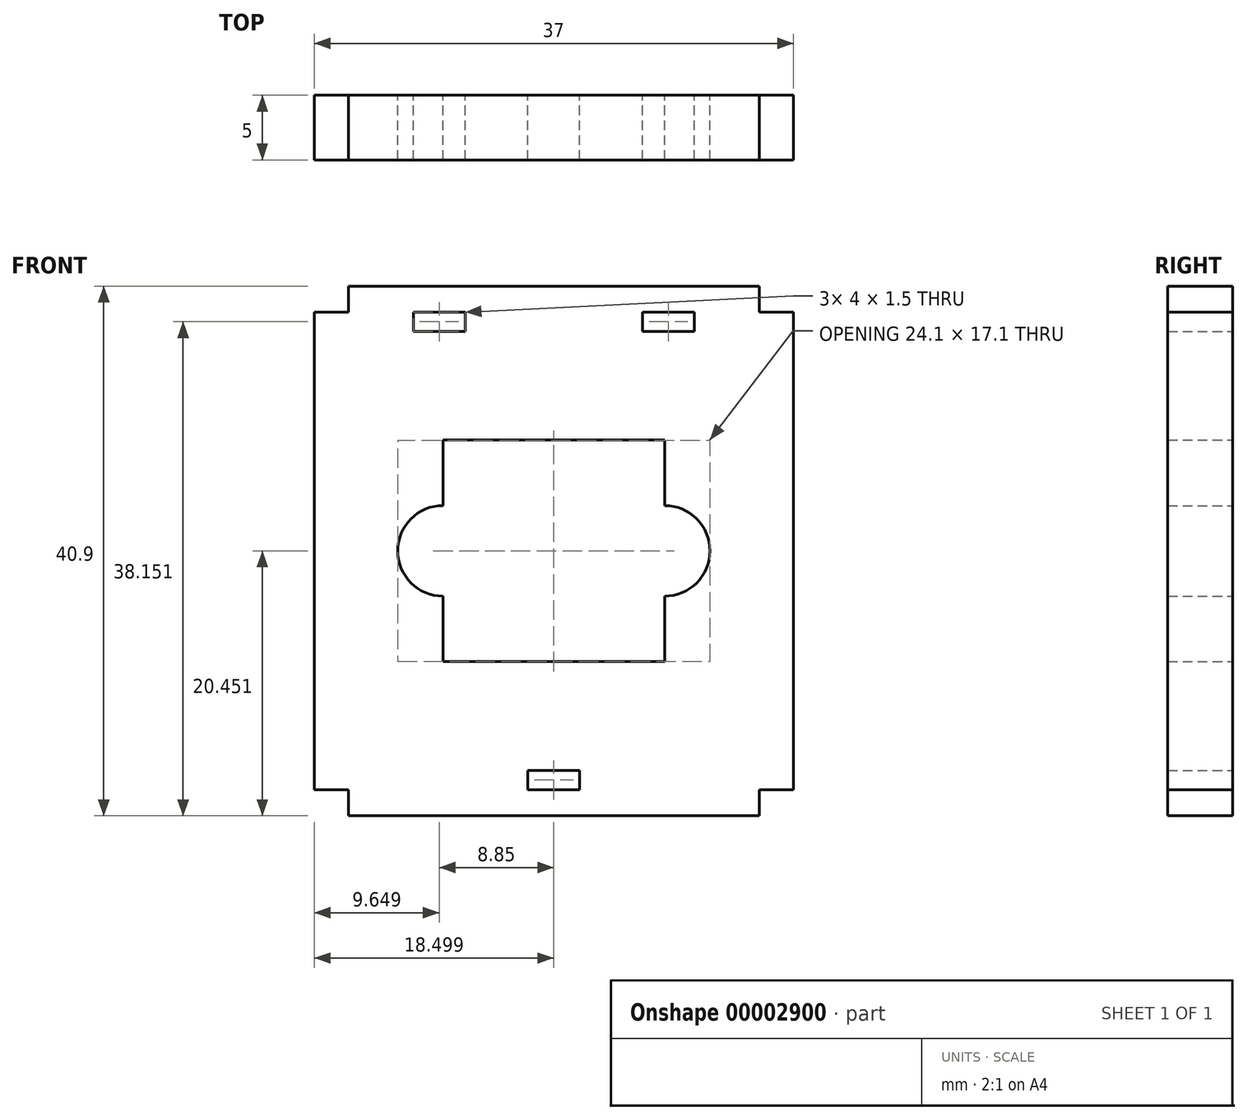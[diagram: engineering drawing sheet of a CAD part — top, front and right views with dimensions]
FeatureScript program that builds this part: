
annotation { "Feature Type Name" : "Feature", "Feature Type Description" : "" }
export const myFeature = defineFeature(function(context is Context, id is Id, definition is map)
    precondition{}
    {
        {
            var Q0;
            Q0=qCreatedBy(makeId("Front.planeOp"),FACE);
            var sketch = newSketch(context, id + "F0", { "sketchPlane" : qUnion([Q0])});
            skLineSegment(sketch, "E0.bottom", {"start": v(-37.5, 13.27) * mm, "end": v(-20.4, 13.27) * mm});
            skLineSegment(sketch, "E0.top", {"start": v(-37.5, -3.83) * mm, "end": v(-20.4, -3.83) * mm});
            skLineSegment(sketch, "E0.left", {"start": v(-37.5, 13.27) * mm, "end": v(-37.5, 8.22) * mm});
            skLineSegment(sketch, "E0.right", {"start": v(-20.4, 13.27) * mm, "end": v(-20.4, 8.22) * mm});
            skArc(sketch, "E1", {"start": v(-37.5, 8.22) * mm, "mid": v(-41, 4.72) * mm, "end": v(-37.5, 1.22) * mm});
            skArc(sketch, "E2", {"start": v(-20.4, 1.22) * mm, "mid": v(-16.9, 4.72) * mm, "end": v(-20.4, 8.22) * mm});
            skLineSegment(sketch, "E3.trimOffspring", {"start": v(-37.5, 1.22) * mm, "end": v(-37.5, -3.83) * mm});
            skLineSegment(sketch, "E4.trimOffspring", {"start": v(-20.4, 1.22) * mm, "end": v(-20.4, -3.83) * mm});
            skLineSegment(sketch, "E5.bottom", {"start": v(-47.45, 23.17) * mm, "end": v(-44.8, 23.17) * mm});
            skLineSegment(sketch, "E5.top", {"start": v(-47.45, -13.73) * mm, "end": v(-44.8, -13.73) * mm});
            skLineSegment(sketch, "E5.left", {"start": v(-47.45, 23.17) * mm, "end": v(-47.45, -13.73) * mm});
            skLineSegment(sketch, "E5.right", {"start": v(-10.45, 23.17) * mm, "end": v(-10.45, -13.73) * mm});
            skLineSegment(sketch, "E6.top", {"start": v(-44.8, 25.17) * mm, "end": v(-13.1, 25.17) * mm});
            skLineSegment(sketch, "E6.left", {"start": v(-44.8, 23.17) * mm, "end": v(-44.8, 25.17) * mm});
            skLineSegment(sketch, "E6.right", {"start": v(-13.1, 23.17) * mm, "end": v(-13.1, 25.17) * mm});
            skLineSegment(sketch, "E7.top", {"start": v(-44.8, -15.73) * mm, "end": v(-13.1, -15.73) * mm});
            skLineSegment(sketch, "E7.left", {"start": v(-44.8, -13.73) * mm, "end": v(-44.8, -15.73) * mm});
            skLineSegment(sketch, "E7.right", {"start": v(-13.1, -13.73) * mm, "end": v(-13.1, -15.73) * mm});
            skLineSegment(sketch, "E8.trimOffspring", {"start": v(-13.1, 23.17) * mm, "end": v(-10.45, 23.17) * mm});
            skLineSegment(sketch, "E9.trimOffspring", {"start": v(-13.1, -13.73) * mm, "end": v(-10.45, -13.73) * mm});
            skLineSegment(sketch, "E10", {"start": v(-28.95, 13.27) * mm, "end": v(-28.95, -3.83) * mm, "construction": true});
            skLineSegment(sketch, "E11.bottom", {"start": v(-39.8, 23.17) * mm, "end": v(-35.8, 23.17) * mm});
            skLineSegment(sketch, "E11.top", {"start": v(-39.8, 21.67) * mm, "end": v(-35.8, 21.67) * mm});
            skLineSegment(sketch, "E11.left", {"start": v(-39.8, 23.17) * mm, "end": v(-39.8, 21.67) * mm});
            skLineSegment(sketch, "E11.right", {"start": v(-35.8, 23.17) * mm, "end": v(-35.8, 21.67) * mm});
            skLineSegment(sketch, "E12.0.MirrorCS", {"start": v(-18.1, 23.17) * mm, "end": v(-22.1, 23.17) * mm});
            skLineSegment(sketch, "E12.1.MirrorCS", {"start": v(-22.1, 23.17) * mm, "end": v(-22.1, 21.67) * mm});
            skLineSegment(sketch, "E12.2.MirrorCS", {"start": v(-18.1, 23.17) * mm, "end": v(-18.1, 21.67) * mm});
            skLineSegment(sketch, "E12.3.MirrorCS", {"start": v(-18.1, 21.67) * mm, "end": v(-22.1, 21.67) * mm});
            skLineSegment(sketch, "E13.bottom", {"start": v(-30.95, -13.73) * mm, "end": v(-26.95, -13.73) * mm});
            skLineSegment(sketch, "E13.top", {"start": v(-30.95, -12.23) * mm, "end": v(-26.95, -12.23) * mm});
            skLineSegment(sketch, "E13.left", {"start": v(-30.95, -13.73) * mm, "end": v(-30.95, -12.23) * mm});
            skLineSegment(sketch, "E13.right", {"start": v(-26.95, -13.73) * mm, "end": v(-26.95, -12.23) * mm});
            skSolve(sketch);
        }
        {
            var Q0;
            Q0 = qSketchRegion(id + "F0", true);
            extrude(context, id + "F1", {"entities" : qUnion([Q0]), "depth" : 5 * mm});
        }
    });
